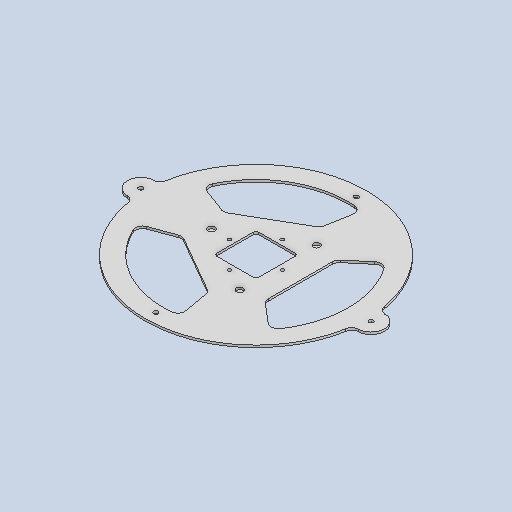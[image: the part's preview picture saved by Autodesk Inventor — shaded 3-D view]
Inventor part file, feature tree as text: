
AUTODESK INVENTOR PART (.ipt)
format: ipt  version: 2025.1 (Build 291241020, 241B)  size: 331,264 bytes
history: native  units: in
note: dims shown in document units (in); Inventor stores cm internally (conversion verified against a paired STEP export)
features: sketch x5, move_body x5, fillet x3, split x3, extrude x2, boolean_combine x1
ambient origin geometry x8: Origin, YZ Plane, XZ Plane, XY Plane, X Axis, Y Axis, Z Axis, Center Point
bodies: Solid25 (feature_tree)
feature tree (19):
  extrude  "Extrusion1"  Depth=2.3661in
  fillet  "Fillet1"  Radius=2.3661in
  extrude  "Extrusion2"  Depth=0.1575in
  fillet  "Fillet2"  Radius=0.1575in
  fillet  "Fillet3"  Radius=0.1575in
  sketch  "Sketch3"  dims[d9=0.201in d10=0.201in d11=2.9921in d12=1.4961in d13=2.9921in d14=1.4961in d15=0.375in d17=4.358in d20=0.375in d24=0.2525in d25=0.2525in d26=11.311in d27=5.6555in d30=1.5in d31=0.2525in d33=13.01in d34=0.125in d35=0.0in d36=0.4in d38=4.358in d39=4.358in d41=5.0322in d42=4.0in d43=2.0in d44=0.8933in d45=0.8933in d46=2.0in d47=2.0in d48=2.5in d49=0.0in d50=1.1811in d52=360.0deg d54=0.25in d55=0.0in d56=0.4in d57=0.4in d58=0.125in d59=1.1811in d61=360.0deg d63=0.125in d64=0.0in d65=2.0in d66=0.0in d67=1.0in d68=4.0in d69=1.0in d70=1.0in d71=0.0in d72=2.0in d73=2.0in d74=-4.0in d75=-1.0in d76=1.0in d77=-2.0in d78=0.0in]
  split  "Split5"
  split  "Split8"
  split  "Split9"
  boolean_combine  "Combine1"
  move_body  "Move Body1"
  move_body  "Move Body2"
  move_body  "Move Body3"
  move_body  "Move Body4"
  move_body  "Move Body5"
  sketch  "Sketch1"  dims[d0=12.5in d1=1.1831in d2=2.3661in]
  sketch  "Sketch2"  dims[d7=0.201in]
  sketch  "Sketch Circular Pattern1"  dims[d3=2.3661in d4=1.1831in d5=0.1575in d6=0.1575in]
  sketch  "Sketch Circular Pattern2"  dims[d8=0.201in]
